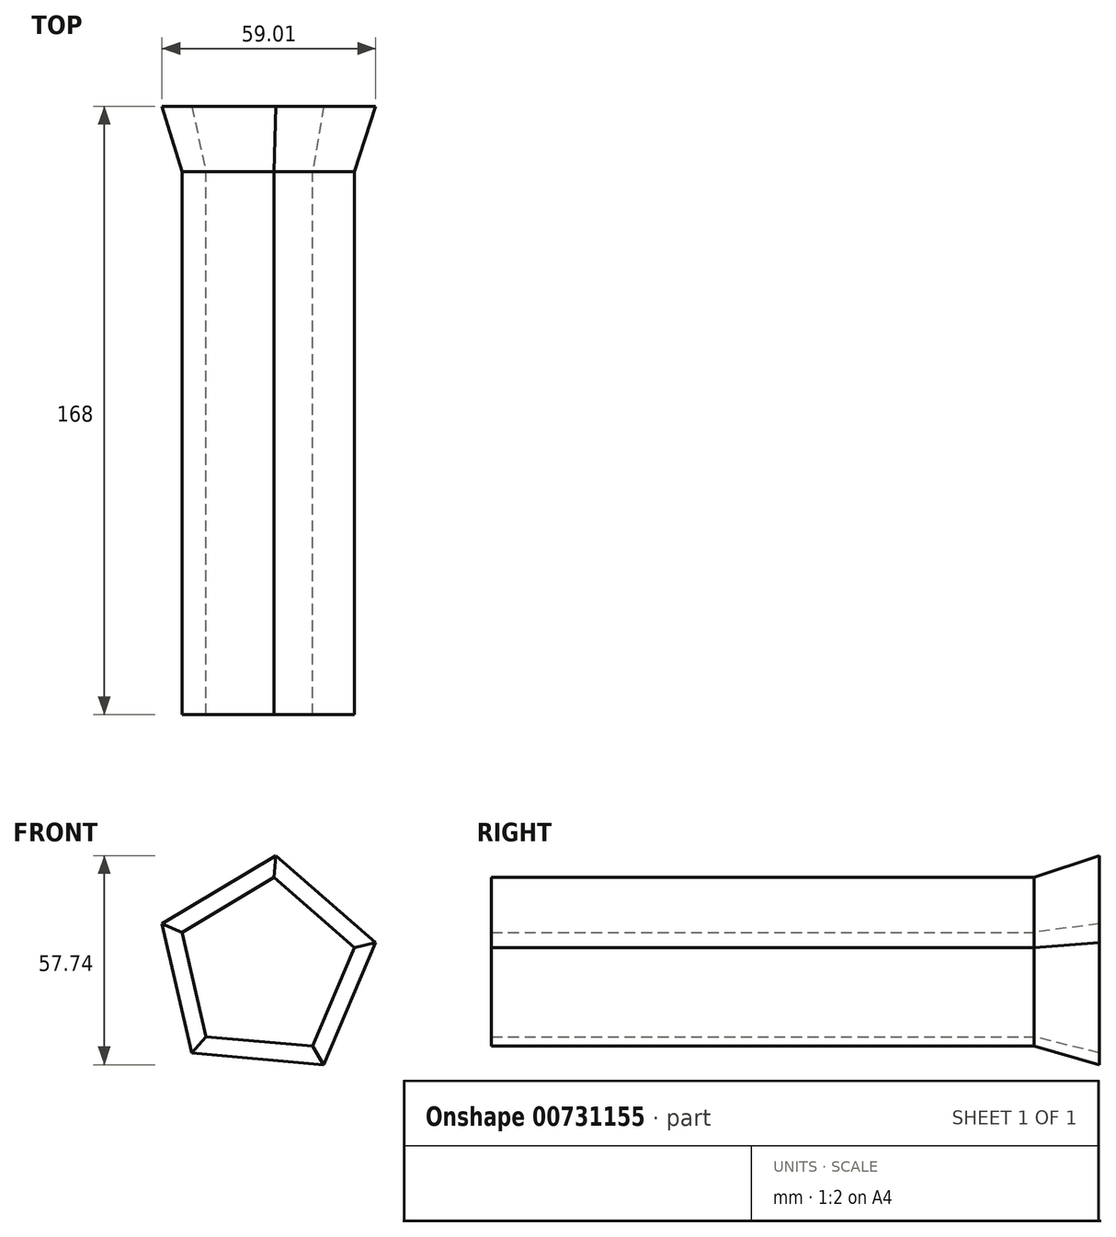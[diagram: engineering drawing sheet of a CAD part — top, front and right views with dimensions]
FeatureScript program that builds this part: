
annotation { "Feature Type Name" : "Feature", "Feature Type Description" : "" }
export const myFeature = defineFeature(function(context is Context, id is Id, definition is map)
    precondition{}
    {
        {
            var Q0;
            Q0=qCreatedBy(makeId("Front.planeOp"),FACE);
            var sketch = newSketch(context, id + "F0", { "sketchPlane" : qUnion([Q0])});
            skLineSegment(sketch, "E0.0", {"start": v(12.4, 36.61) * mm, "end": v(34.72, 17.16) * mm});
            skLineSegment(sketch, "E0.1", {"start": v(34.72, 17.16) * mm, "end": v(23.12, -10.08) * mm});
            skLineSegment(sketch, "E0.2", {"start": v(23.12, -10.08) * mm, "end": v(-6.37, -7.46) * mm});
            skLineSegment(sketch, "E0.3", {"start": v(-6.37, -7.46) * mm, "end": v(-13, 21.4) * mm});
            skLineSegment(sketch, "E0.4", {"start": v(-13, 21.4) * mm, "end": v(12.4, 36.61) * mm});
            skSolve(sketch);
        }
        {
            var Q0;
            Q0=makeQuery(id+"F0.imprint","IMPRINT",FACE,{"disambiguationData":[TD([[makeQuery(id+"F0.imprint","IMPRINT",EDGE,{"derivedFrom":sQuery(id+"F0.wireOp",EDGE,"E0.0")}),-1.0]])]});
            extrude(context, id + "F1", {"entities" : qUnion([Q0]), "depth" : 150 * mm, "offsetDistance" : 25 * mm});
        }
        {
            var Q0;
            Q0=makeQuery(id+"F1.opExtrude","CAP_FACE",FACE,{"disambiguationData":[OSD([sQuery(id+"F0.wireOp",EDGE,"E0.0"),sQuery(id+"F0.wireOp",EDGE,"E0.1"),sQuery(id+"F0.wireOp",EDGE,"E0.2"),sQuery(id+"F0.wireOp",EDGE,"E0.3"),sQuery(id+"F0.wireOp",EDGE,"E0.4")])],"isStart":true});
            extrude(context, id + "F2", {"entities" : qUnion([Q0]), "operationType" : NewBodyOperationType.ADD, "depth" : 18 * mm, "offsetDistance" : 25 * mm, "hasDraft" : true, "draftAngle" : 15 * degree});
        }
    });
